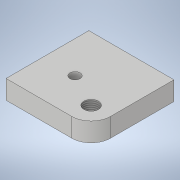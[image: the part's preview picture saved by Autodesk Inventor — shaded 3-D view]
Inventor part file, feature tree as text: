
AUTODESK INVENTOR PART (.ipt)
format: ipt  version: 2021 (Build 250183000, 183)  size: 117,760 bytes
history: native  units: mm
features: sketch x5, hole x2, extrude x1, fillet x1
ambient origin geometry x8: Origin, YZ Plane, XZ Plane, XY Plane, X Axis, Y Axis, Z Axis, Center Point
bodies: Body1 (feature_tree)
feature tree (9):
  extrude  "Выдавливание2"  TaperAngle=0.0deg  [1 undecoded]
  fillet  "Сопряжение1"  Radius=42.0mm
  hole  "Отверстие5"  [1 undecoded]
  hole  "Отверстие7"  [1 undecoded]
  sketch  "Эскиз1"
  sketch  "Эскиз2"
  sketch  "Эскиз3"
  sketch  "Эскиз5"
  sketch  "Эскиз7"
note: 3 required parameter values undecoded (feature->parameter linkage not recoverable at this tier; creation-order binding heuristic only, values carry confidence <= 0.55)
